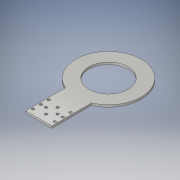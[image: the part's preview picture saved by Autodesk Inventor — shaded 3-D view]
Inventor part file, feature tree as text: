
AUTODESK INVENTOR PART (.ipt)
format: ipt  version: 2016 (Build 200138000, 138)  size: 166,400 bytes
history: native  units: mm
features: sketch x2, extrude x1, hole x1, projected_geometry x1
ambient origin geometry x8: Origin, YZ Plane, XZ Plane, XY Plane, X Axis, Y Axis, Z Axis, Center Point
bodies: Solid1 (feature_tree)
feature tree (5):
  extrude  "Extrusion1"  Depth=38.1mm
  hole  "Hole1"  [1 undecoded]
  sketch  "Sketch1"  dims[d0=38.1mm d1=38.1mm]
  sketch  "Sketch2"  dims[d2=25.4mm d3=63.5mm d4=95.25mm d5=57.15mm d6=3.175mm d7=0.0mm d8=38.1mm d9=38.1mm d10=31.75mm d11=22.86mm d12=22.86mm d13=31.75mm d14=11.938mm d15=11.938mm d16=16.882882mm d17=16.882882mm d18=4.445mm d19=7.433559mm d20=5.969mm d21=5.969mm d22=4.445mm d23=7.433559mm d24=9.906mm d25=9.906mm d26=21.844mm d27=21.844mm d28=3.175mm d29=27.491441mm d30=3.7973mm d31=19.05mm d32=9.525mm d33=6.35mm d34=14.3117mm d35=25.4mm d36=20.594885mm]
  projected_geometry  "Projected Loop1"
note: 1 required parameter value undecoded (feature->parameter linkage not recoverable at this tier; creation-order binding heuristic only, values carry confidence <= 0.55)
